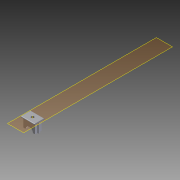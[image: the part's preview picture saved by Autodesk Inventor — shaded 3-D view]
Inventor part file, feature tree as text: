
AUTODESK INVENTOR PART (.ipt)
format: ipt  version: 2012 (Build 160160000, 160)  size: 252,928 bytes
history: native  units: in
note: dims shown in document units (in); Inventor stores cm internally (conversion verified against a paired STEP export)
features: sketch x8, extrude x8, reference x5, projected_geometry x5, fillet x3, plane x2, other x1
ambient origin geometry x8: Origin, YZ Plane, XZ Plane, XY Plane, X Axis, Y Axis, Z Axis, Center Point
feature tree (32):
  plane  "Work Plane8"
  sketch  "Sketch21"  dims[d99=0.0118in d100=0.0118in]
  plane  "Work Plane9"
  extrude  "Extrusion20"  Depth=0.0118in
  extrude  "Extrusion21"  Depth=0.0118in
  extrude  "Extrusion22"  Depth=0.0118in
  extrude  "Extrusion23"  Depth=0.0118in
  sketch  "Sketch25"  dims[d108=0.0118in d109=0.0118in d110=0.0118in d111=0.3937in d112=0.0in]
  fillet  "Fillet13"  Radius=0.0118in
  extrude  "Extrusion24"  Depth=0.0118in
  fillet  "Fillet14"  Radius=0.0118in
  fillet  "Fillet15"  Radius=0.3937in
  extrude  "Extrusion25"  Depth=0.0984in
  extrude  "Extrusion26"  Depth=0.0118in
  extrude  "Extrusion27"  Depth=0.0591in TaperAngle=0.0deg
  other  "Work Axis1"
  reference  "Reference41"
  sketch  "Sketch22"  dims[d101=0.0118in d102=0.0118in]
  reference  "Reference42"
  sketch  "Sketch23"  dims[d103=0.0118in d104=0.0118in]
  projected_geometry  "Projected Loop8"
  reference  "Reference43"
  reference  "Reference44"
  sketch  "Sketch24"  dims[d105=0.0118in d106=0.0118in d107=0.0118in]
  projected_geometry  "Projected Loop9"
  reference  "Reference45"
  sketch  "Sketch26"  dims[d113=0.3937in d114=0.0in d115=0.0984in]
  projected_geometry  "Projected Loop10"
  projected_geometry  "Projected Loop11"
  sketch  "Sketch27"  dims[d116=0.0984in d117=0.0118in]
  projected_geometry  "Projected Loop12"
  sketch  "Sketch28"  dims[d118=0.0118in d119=0.0591in d120=0.0in d121=0.8016in d122=0.2672in d123=0.2672in d124=0.0295in d125=0.0591in d126=0.0591in d127=0.0in d128=0.0787in d129=0.0591in d130=0.0in d131=0.0787in d132=0.0394in d133=0.0059in d134=0.0in d135=0.0059in d136=0.0in d137=0.1969in d138=0.0in]
